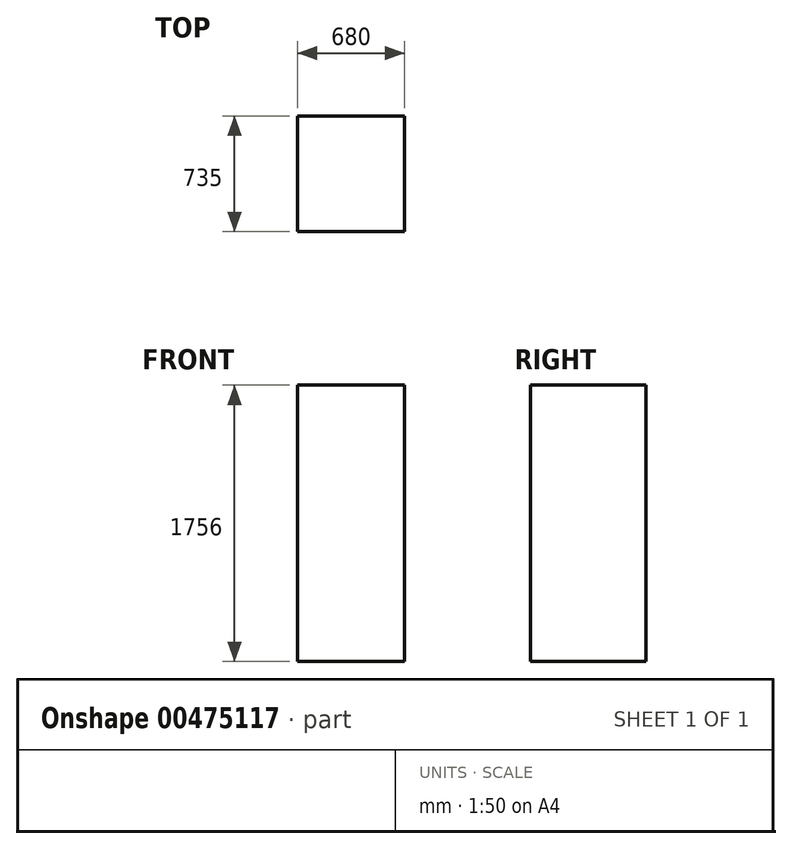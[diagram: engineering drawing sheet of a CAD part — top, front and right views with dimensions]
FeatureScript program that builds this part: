
annotation { "Feature Type Name" : "Feature", "Feature Type Description" : "" }
export const myFeature = defineFeature(function(context is Context, id is Id, definition is map)
    precondition{}
    {
        {
            var Q0;
            Q0=qCreatedBy(makeId("Top.planeOp"),FACE);
            var sketch = newSketch(context, id + "F0", { "sketchPlane" : qUnion([Q0])});
            skLineSegment(sketch, "E0.bottom", {"start": v(340, 367.5) * mm, "end": v(-340, 367.5) * mm});
            skLineSegment(sketch, "E0.top", {"start": v(340, -367.5) * mm, "end": v(-340, -367.5) * mm});
            skLineSegment(sketch, "E0.left", {"start": v(340, 367.5) * mm, "end": v(340, -367.5) * mm});
            skLineSegment(sketch, "E0.right", {"start": v(-340, 367.5) * mm, "end": v(-340, -367.5) * mm});
            skPoint(sketch, "E0.middle", {"position": v(0, 0) * mm});
            skSolve(sketch);
        }
        {
            var Q0;
            Q0 = qSketchRegion(id + "F0", true);
            extrude(context, id + "F1", {"entities" : qUnion([Q0]), "depth" : 1756 * mm, "offsetDistance" : 25 * mm});
        }
    });
